# Revit family: LeL Colorado 7.2
name_source: partatom
category: Lighting Fixtures
units: mm (PartAtom-declared; Revit-internal decimal feet)

## family parameters
Cut with Voids When Loaded = Yes
Host = Face
Light Source = No
Part Type = Normal
Room Calculation Point = No
Round Connector Dimension = Use Diameter
Shared = No

## types (5) — shared parameters
Accessories = WCCA12A0T
Alimentazione = 230 V
Apparent Load = 85 VA
CCT = 3500 K
CRI = 80
Default Elevation = 1219 mm
Description = Outdoor Linear Profile
Finish = LeL Black
IK = IK10
IP = IP65 IP67 IP69
Lamp = LED
Lenght = 1225 mm
Manufacturer = L&L Luce&Light
Model = CA72
Outercasing = 1265 mm
Rated Power supply = 230 V
URL = https://www.lucelight.it
Wattage = 85 W
Weight = 10.50 kg

## per-type parameters (varying)
| type | Optic |
| 7.2 W 16°x66° 85W | COLORADO Light source : 7.2 W 16°x66° 85W |
| 7.2 D 85W | COLORADO Light source : 7.2 D 85W |
| 7.2 L 36° 85W | COLORADO Light source : 7.2 L 36° 85W |
| 7.2 M 26° 85W | COLORADO Light source : 7.2 M 26° 85W |
| 7.2 S 16° 85W | COLORADO Light source : 7.2 S 16° 85W |

## geometry (parser evidence)
native form markers: Sweep x4
no freeform markers — native parametric forms only
